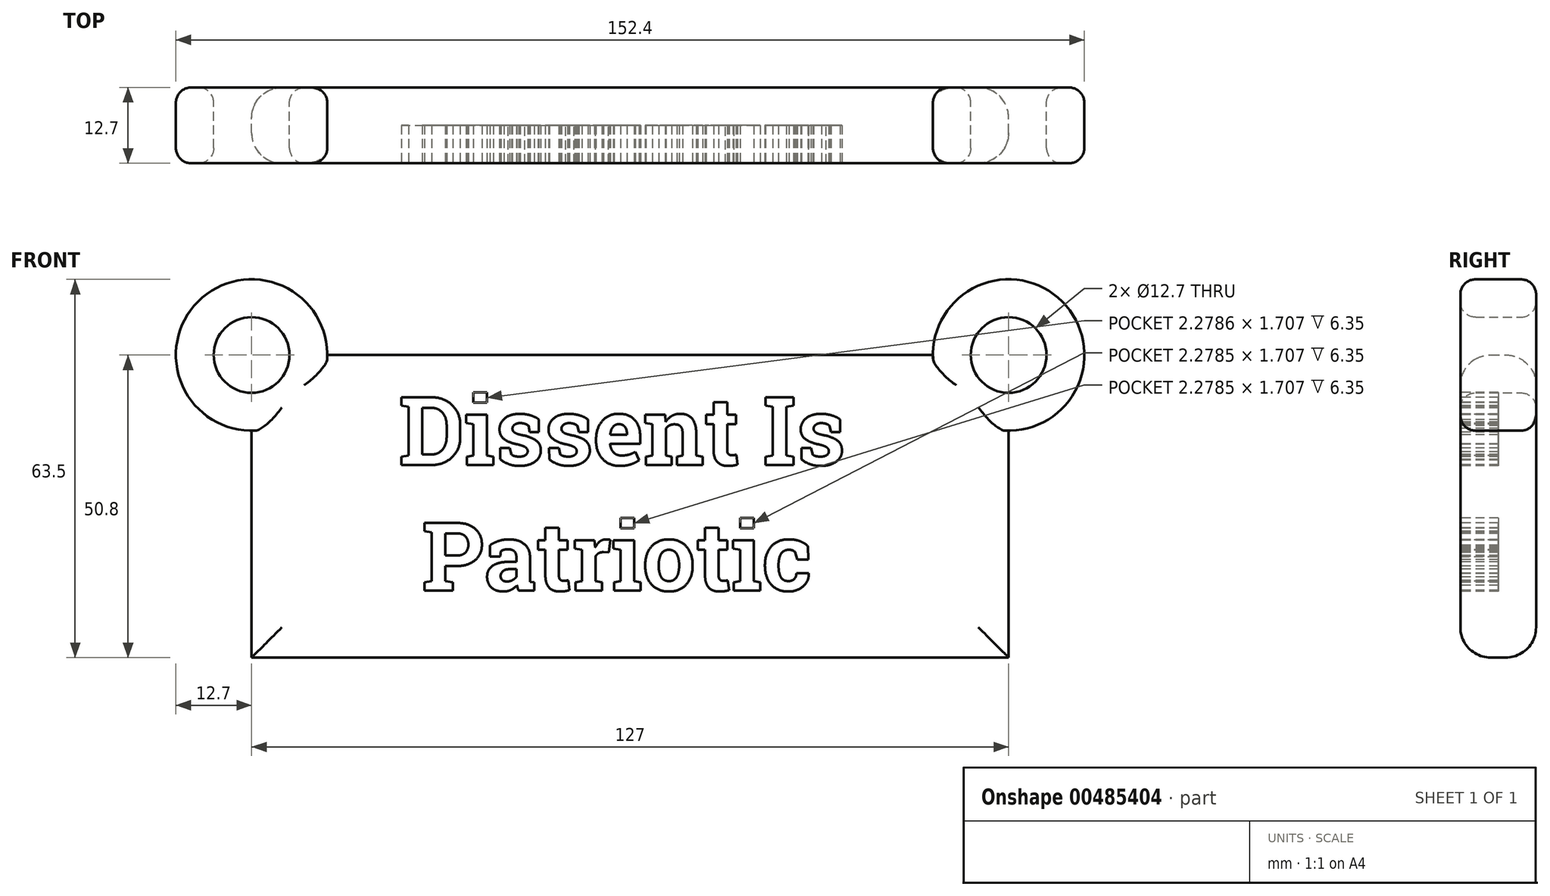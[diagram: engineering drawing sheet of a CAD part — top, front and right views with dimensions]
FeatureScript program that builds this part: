
annotation { "Feature Type Name" : "Feature", "Feature Type Description" : "" }
export const myFeature = defineFeature(function(context is Context, id is Id, definition is map)
    precondition{}
    {
        {
            var Q0;
            Q0=qCreatedBy(makeId("Front.planeOp"),FACE);
            var sketch = newSketch(context, id + "F0", { "sketchPlane" : qUnion([Q0])});
            skLineSegment(sketch, "E0.bottom", {"start": v(-127, 50.8) * mm, "end": v(0, 50.8) * mm});
            skLineSegment(sketch, "E0.top", {"start": v(-127, 0) * mm, "end": v(0, 0) * mm});
            skLineSegment(sketch, "E0.left", {"start": v(-127, 50.8) * mm, "end": v(-127, 0) * mm});
            skLineSegment(sketch, "E0.right", {"start": v(0, 50.8) * mm, "end": v(0, 0) * mm});
            skCircle(sketch, "E1", {"center": v(-127, 50.8) * mm, "radius": 6.35 * mm});
            skCircle(sketch, "E2", {"center": v(0, 50.8) * mm, "radius": 12.7 * mm});
            skCircle(sketch, "E3", {"center": v(0, 50.8) * mm, "radius": 6.35 * mm});
            skCircle(sketch, "E4", {"center": v(-127, 50.8) * mm, "radius": 12.7 * mm});
            skSolve(sketch);
        }
        {
            var Q0;
            Q0 = qSketchRegion(id + "F0", true);
            extrude(context, id + "F1", {"entities" : qUnion([Q0]), "depth" : 12.7 * mm});
        }
        {
            var Q0;
            Q0=makeQuery(id+"F1.opExtrude","CAP_FACE",FACE,{"disambiguationData":[OSD([sQuery(id+"F0.wireOp",EDGE,"E0.bottom"),sQuery(id+"F0.wireOp",EDGE,"E0.top"),sQuery(id+"F0.wireOp",EDGE,"E0.left"),sQuery(id+"F0.wireOp",EDGE,"E0.right"),sQuery(id+"F0.wireOp",EDGE,"E1"),sQuery(id+"F0.wireOp",EDGE,"E2"),sQuery(id+"F0.wireOp",EDGE,"E3"),sQuery(id+"F0.wireOp",EDGE,"E4")])],"isStart":false});
            var sketch = newSketch(context, id + "F2", { "sketchPlane" : qUnion([Q0])});
            skText(sketch, "E5", { "text": "Dissent Is\n Patriotic", "fontName": "RobotoSlab-Bold.ttf"});
            const initialGuessF2  = {"E5": [-0.10232, 0.03234, 1, 0, 0.0115]};
            skSetInitialGuess(sketch, initialGuessF2);
            skSolve(sketch);
        }
        {
            var Q0;
            Q0 = qSketchRegion(id + "F2", true);
            extrude(context, id + "F3", {"entities" : qUnion([Q0]), "operationType" : NewBodyOperationType.REMOVE, "oppositeDirection" : true, "depth" : 6.35 * mm});
        }
        {
            var Q0;
            Q0=makeQuery(id+"F1.opExtrude","CAP_EDGE",EDGE,{"disambiguationData":[OSD([sQuery(id+"F0.wireOp",EDGE,"E1")])],"isStart":false});
            var Q1;
            Q1=makeQuery(id+"F1.opExtrude","CAP_EDGE",EDGE,{"disambiguationData":[OSD([sQuery(id+"F0.wireOp",EDGE,"E3")])],"isStart":false});
            var Q2;
            Q2=makeQuery(id+"F1.opExtrude","CAP_EDGE",EDGE,{"disambiguationData":[OSD([sQuery(id+"F0.wireOp",EDGE,"E1")])],"isStart":true});
            var Q3;
            Q3=makeQuery(id+"F1.opExtrude","CAP_EDGE",EDGE,{"disambiguationData":[OSD([sQuery(id+"F0.wireOp",EDGE,"E3")])],"isStart":true});
            var Q4;
            Q4=makeQuery(id+"F1.opExtrude","CAP_EDGE",EDGE,{"disambiguationData":[OSD([sQuery(id+"F0.wireOp",EDGE,"E4")])],"isStart":false});
            var Q5;
            Q5=makeQuery(id+"F1.opExtrude","CAP_EDGE",EDGE,{"disambiguationData":[OSD([sQuery(id+"F0.wireOp",EDGE,"E4")])],"isStart":true});
            var Q6;
            Q6=makeQuery(id+"F1.opExtrude","CAP_EDGE",EDGE,{"disambiguationData":[OSD([sQuery(id+"F0.wireOp",EDGE,"E2")])],"isStart":true});
            var Q7;
            Q7=makeQuery(id+"F1.opExtrude","CAP_EDGE",EDGE,{"disambiguationData":[OSD([sQuery(id+"F0.wireOp",EDGE,"E2")])],"isStart":false});
            fillet(context, id + "F4", {"entities" : qUnion([Q0, Q1, Q2, Q3, Q4, Q5, Q6, Q7]), "radius" : 2.54 * mm, "tangentPropagation" : true, "allowEdgeOverflow" : false});
        }
        {
            var Q0;
            Q0=makeQuery(id+"F1.opExtrude","CAP_EDGE",EDGE,{"disambiguationData":[OSD([sQuery(id+"F0.wireOp",EDGE,"E0.bottom")])],"isStart":false});
            var Q1;
            Q1=makeQuery(id+"F1.opExtrude","CAP_EDGE",EDGE,{"disambiguationData":[OSD([sQuery(id+"F0.wireOp",EDGE,"E0.bottom")])],"isStart":true});
            var Q2;
            Q2=makeQuery(id+"F1.opExtrude","CAP_EDGE",EDGE,{"disambiguationData":[OSD([sQuery(id+"F0.wireOp",EDGE,"E0.right")])],"isStart":false});
            var Q3;
            Q3=makeQuery(id+"F1.opExtrude","CAP_EDGE",EDGE,{"disambiguationData":[OSD([sQuery(id+"F0.wireOp",EDGE,"E0.right")])],"isStart":true});
            var Q4;
            Q4=makeQuery(id+"F1.opExtrude","CAP_EDGE",EDGE,{"disambiguationData":[OSD([sQuery(id+"F0.wireOp",EDGE,"E0.top")])],"isStart":false});
            var Q5;
            Q5=makeQuery(id+"F1.opExtrude","CAP_EDGE",EDGE,{"disambiguationData":[OSD([sQuery(id+"F0.wireOp",EDGE,"E0.left")])],"isStart":false});
            var Q6;
            Q6=makeQuery(id+"F1.opExtrude","CAP_EDGE",EDGE,{"disambiguationData":[OSD([sQuery(id+"F0.wireOp",EDGE,"E0.top")])],"isStart":true});
            var Q7;
            Q7=makeQuery(id+"F1.opExtrude","CAP_EDGE",EDGE,{"disambiguationData":[OSD([sQuery(id+"F0.wireOp",EDGE,"E0.left")])],"isStart":true});
            fillet(context, id + "F5", {"entities" : qUnion([Q0, Q1, Q2, Q3, Q4, Q5, Q6, Q7]), "radius" : 5.08 * mm, "tangentPropagation" : true, "allowEdgeOverflow" : false});
        }
    });
